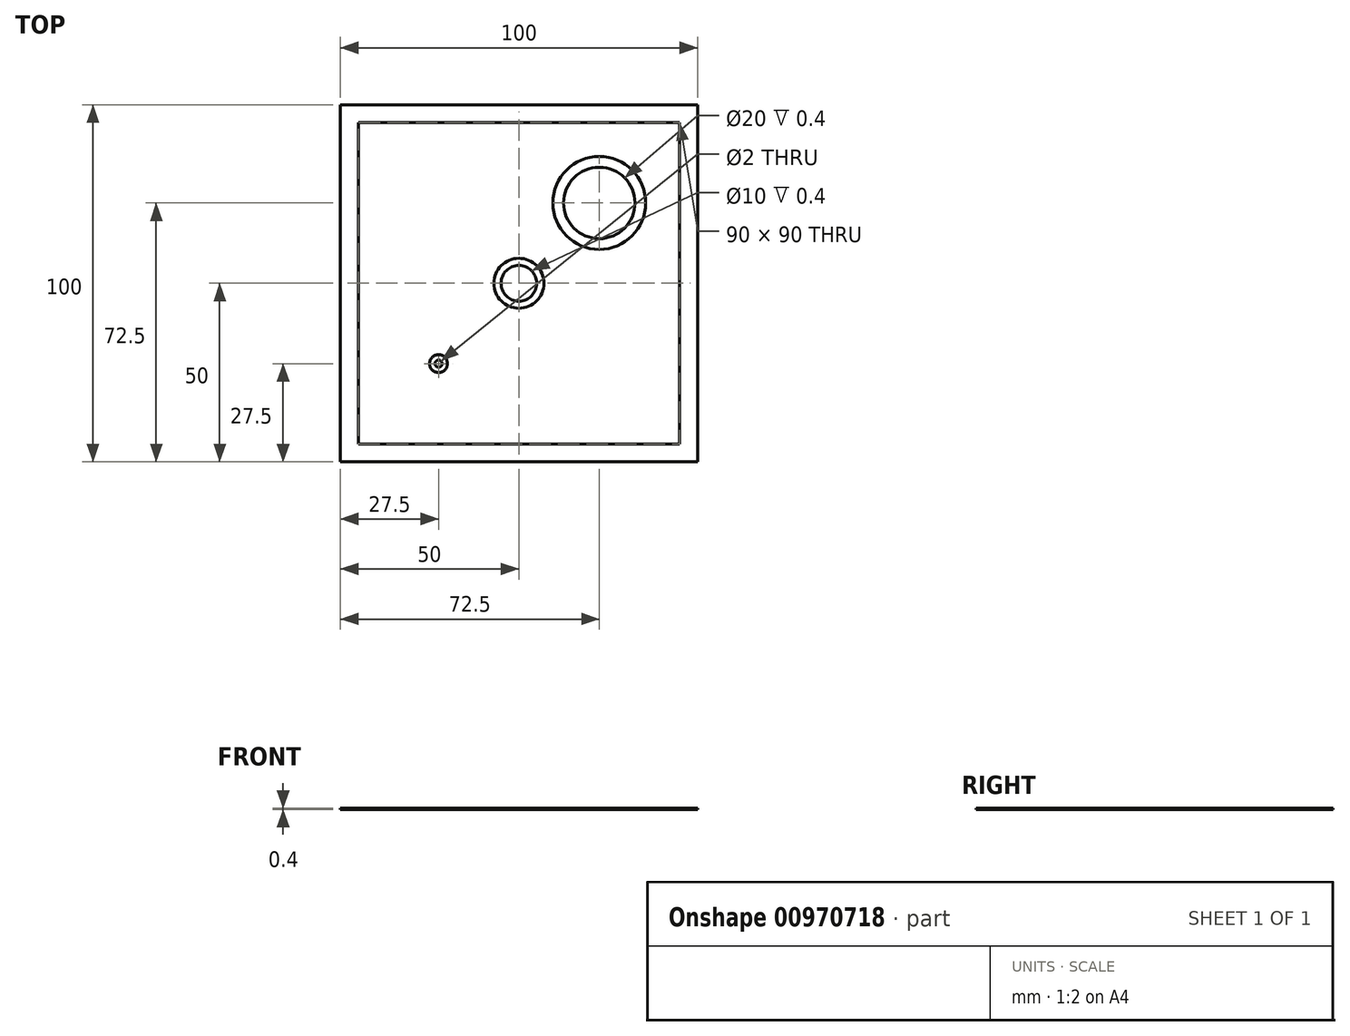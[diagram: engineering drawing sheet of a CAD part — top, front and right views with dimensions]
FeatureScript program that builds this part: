
annotation { "Feature Type Name" : "Feature", "Feature Type Description" : "" }
export const myFeature = defineFeature(function(context is Context, id is Id, definition is map)
    precondition{}
    {
        {
            var Q0;
            Q0=qCreatedBy(makeId("Top.planeOp"),FACE);
            var sketch = newSketch(context, id + "F0", { "sketchPlane" : qUnion([Q0])});
            skLineSegment(sketch, "E0.bottom", {"start": v(45, -45) * mm, "end": v(-45, -45) * mm});
            skLineSegment(sketch, "E0.top", {"start": v(45, 45) * mm, "end": v(-45, 45) * mm});
            skLineSegment(sketch, "E0.left", {"start": v(45, -45) * mm, "end": v(45, 45) * mm});
            skLineSegment(sketch, "E0.right", {"start": v(-45, -45) * mm, "end": v(-45, 45) * mm});
            skPoint(sketch, "E0.middle", {"position": v(0, 0) * mm});
            skLineSegment(sketch, "E1.0", {"start": v(50, 50) * mm, "end": v(-50, 50) * mm});
            skLineSegment(sketch, "E1.1", {"start": v(50, -50) * mm, "end": v(50, 50) * mm});
            skLineSegment(sketch, "E1.2", {"start": v(50, -50) * mm, "end": v(-50, -50) * mm});
            skLineSegment(sketch, "E1.3", {"start": v(-50, -50) * mm, "end": v(-50, 50) * mm});
            skCircle(sketch, "E2", {"center": v(-22.5, -22.5) * mm, "radius": 1 * mm});
            skCircle(sketch, "E3", {"center": v(0, 0) * mm, "radius": 5 * mm});
            skCircle(sketch, "E4", {"center": v(22.5, 22.5) * mm, "radius": 10 * mm});
            skLineSegment(sketch, "E5", {"start": v(-45, -45) * mm, "end": v(0, 0) * mm, "construction": true});
            skLineSegment(sketch, "E6", {"start": v(0, 0) * mm, "end": v(45, 45) * mm, "construction": true});
            skCircle(sketch, "E7", {"center": v(-22.5, -22.5) * mm, "radius": 2.5 * mm});
            skCircle(sketch, "E8", {"center": v(0, 0) * mm, "radius": 7 * mm});
            skCircle(sketch, "E9", {"center": v(22.5, 22.5) * mm, "radius": 13 * mm});
            skSolve(sketch);
        }
        {
            var Q0;
            Q0 = qSketchRegion(id + "F0", true);
            var Q1;
            Q1=makeQuery(id+"F0.imprint","IMPRINT",FACE,{"disambiguationData":[TD([[makeQuery(id+"F0.imprint","IMPRINT",EDGE,{"derivedFrom":sQuery(id+"F0.wireOp",EDGE,"E2")}),-1.0]])]});
            var Q2;
            Q2=makeQuery(id+"F0.imprint","IMPRINT",FACE,{"disambiguationData":[TD([[makeQuery(id+"F0.imprint","IMPRINT",EDGE,{"derivedFrom":sQuery(id+"F0.wireOp",EDGE,"E3")}),-1.0]])]});
            var Q3;
            Q3=makeQuery(id+"F0.imprint","IMPRINT",FACE,{"disambiguationData":[TD([[makeQuery(id+"F0.imprint","IMPRINT",EDGE,{"derivedFrom":sQuery(id+"F0.wireOp",EDGE,"E4")}),-1.0]])]});
            extrude(context, id + "F1", {"entities" : qUnion([Q0, Q1, Q2, Q3]), "depth" : 0.4 * mm, "offsetDistance" : 25 * mm});
        }
    });
